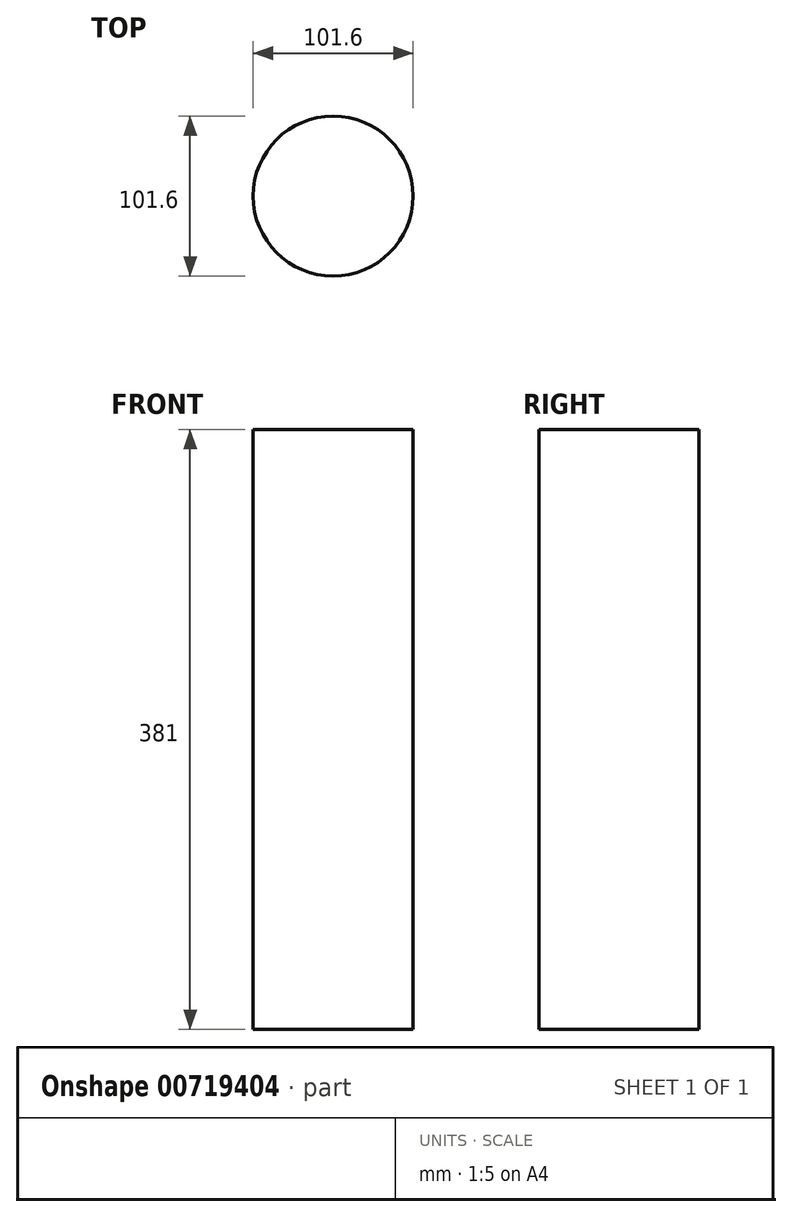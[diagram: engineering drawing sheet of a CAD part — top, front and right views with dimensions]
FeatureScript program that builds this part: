
annotation { "Feature Type Name" : "Feature", "Feature Type Description" : "" }
export const myFeature = defineFeature(function(context is Context, id is Id, definition is map)
    precondition{}
    {
        {
            var Q0;
            Q0=qCreatedBy(makeId("Top.planeOp"),FACE);
            var sketch = newSketch(context, id + "F0", { "sketchPlane" : qUnion([Q0])});
            skCircle(sketch, "E0", {"center": v(0, 0) * mm, "radius": 50.8 * mm});
            skSolve(sketch);
        }
        {
            var Q0;
            Q0 = qSketchRegion(id + "F0", true);
            extrude(context, id + "F1", {"entities" : qUnion([Q0]), "depth" : 381 * mm, "offsetDistance" : 25.4 * mm});
        }
    });
